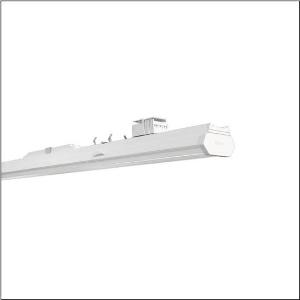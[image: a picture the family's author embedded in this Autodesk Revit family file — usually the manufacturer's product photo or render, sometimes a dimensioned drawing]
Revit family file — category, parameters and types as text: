
# Revit family: licross_r__11_protected_mo_51tp12dn495g3c_6ec9
name_source: partatom
category: Lighting Fixtures
units: mm (PartAtom-declared; Revit-internal decimal feet)

## family parameters
Cut with Voids When Loaded = No
Host = Face
Light Source = No
Part Type = Normal
Room Calculation Point = No
Round Connector Dimension = Use Diameter
Shared = No

## types (1)
- --- (1 x LED, 980 lm, 6.8 W, 4000K)
    Apparent Load = 7 VA
    CIE Flux Codes = 73 92 98 99 100
    Color Rendering = 80
    Color Temperature = 4000K
    Default Elevation = 1800 mm
    Description = Licross® 11 Protected MO, luminaire insert, of sheet steel, galvanised, coil coated, white, length: 1.500mm, width: 90mm, height: 101mm, LED rated luminous flux: 9.980lm, light colour: 840, control gear: DALI 2, with plug, 6-pole, with phase selection, for trunking rail, 14-core, mains connection: 220..240V, AC, 50/60Hz, rated input power: 61W, for trunking rail, 14-core, halogen-free wiring, for emergency light function, converter,control gear: single battery element, battery: LiFeP04, 9Ah, primary light control with lens, of plastic, primary optical cover: cover, of PMMA, light emission: direct distribution, primary light characteristic: symmetric, protection rating (complete): IP64, insulation class (complete): insulation class I (protective earthing), certification: CE, UKCA, protection symbol: D if used in an environment with conductive dust loads with corresponding accessories, impact resistance: IK06, permissible ambient temperature for indoor applications: +5..+35°C, standard: EN 60598-2-22, LABS conformity tested according to VDMA 24364:2018-05, reducing of maximum allowable ambient temperature of 5°C with ceiling mounting, corresponds to IFS (International Featured Standards) requirements for safety and quality in the food industry, packaging unit: 1 piece
    Height = 92 mm
    Lamp = 1 x LED
    Lamp Light Flux = 980 lm
    Lamp Power = 6.8 W
    Lamp count = 1
    Length = 1500 mm
    Luminous efficacy = 144 lm/W
    Manufacturer = Siteco
    ModVariant = No
    Model = 51TP12DN495G3C
    Mounting Place = Ceiling
    Mounting Type = Pendant
    Number of Poles = 1
    OnlyDefault = Yes
    Power Factor = 1
    Product Name = Licross® 11 Protected MO
    Product group = luminaire insert
    ProductGroupID = 901
    Protection Class = Protection class I
    Protection Degree = IP 64
    RLX_Detail_Level = 1
    RLX_Emergency_Light_Flux = 0 lm
    RLX_Emergency_Type = 0
    RLX_Emergency_Type_DB = No
    RlxData = <blob elided: 24661 chars, md5=b4f302b5>
    Socket = socket
    Standby Power = 0 W
    System Light Flux = 980 lm
    System Power = 7 W
    Type Comments = : emergency light operation: 3 h
    Type Image = l_1256148.jpg
    URL = http://relux.com
    VarID = @adj_023057
    Voltage = 0 V
    Weight = 0.00 kg
    Width = 88 mm

## geometry (parser evidence)
native form markers: Blend x4, Sweep x11
no freeform markers — native parametric forms only
